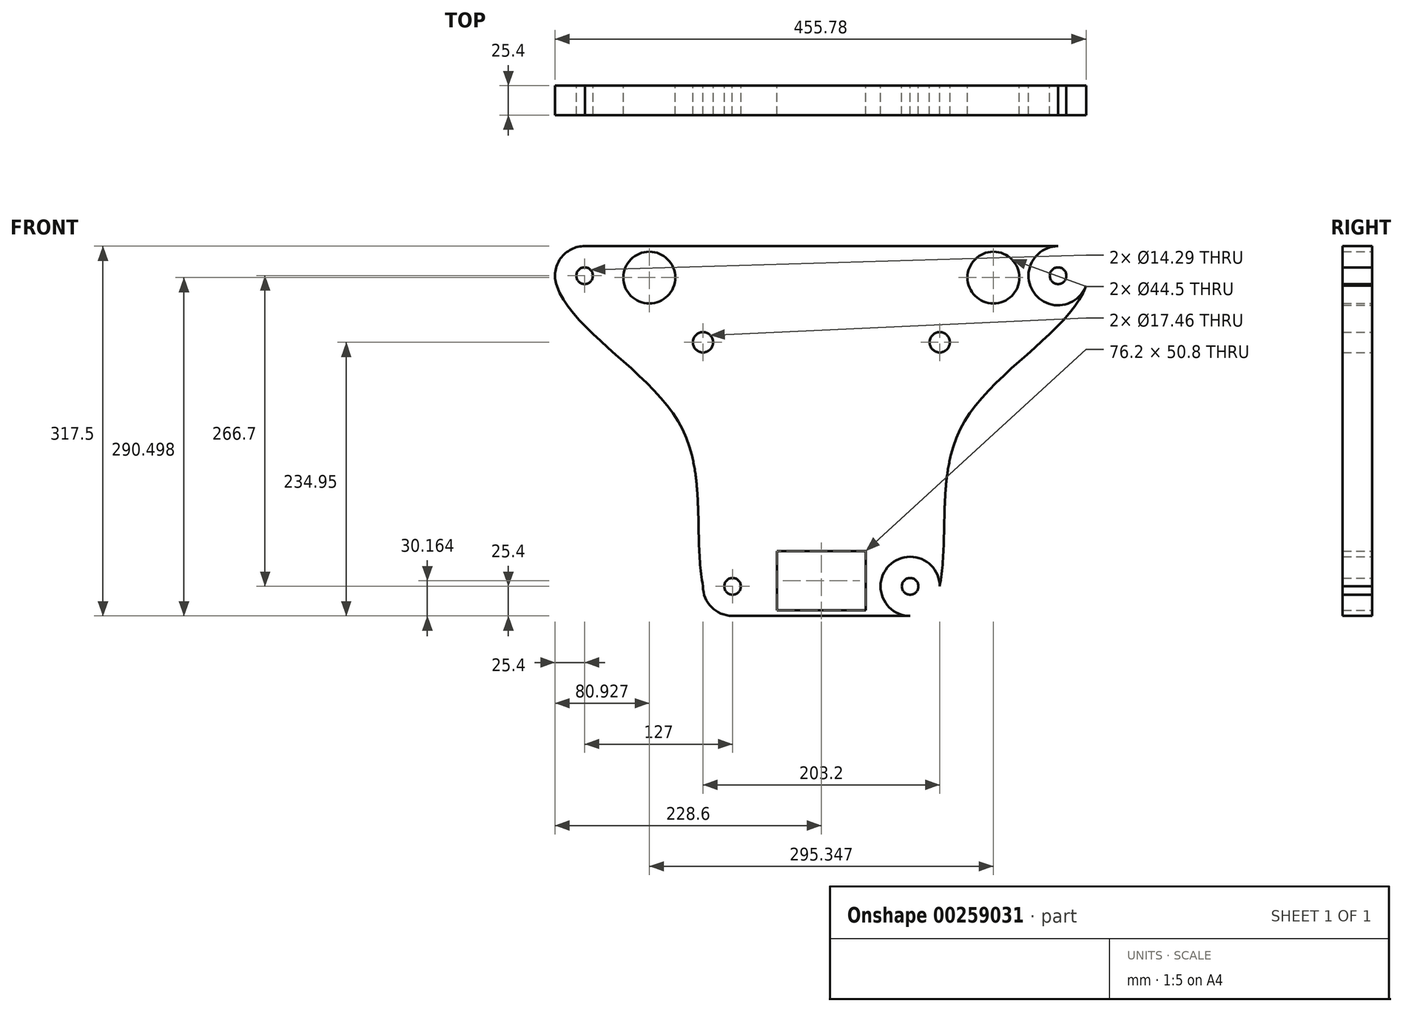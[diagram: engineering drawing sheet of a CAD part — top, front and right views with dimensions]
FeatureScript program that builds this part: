
annotation { "Feature Type Name" : "Feature", "Feature Type Description" : "" }
export const myFeature = defineFeature(function(context is Context, id is Id, definition is map)
    precondition{}
    {
        {
            var Q0;
            Q0=qCreatedBy(makeId("Front.planeOp"),FACE);
            var sketch = newSketch(context, id + "F0", { "sketchPlane" : qUnion([Q0])});
            skCircle(sketch, "E0", {"center": v(-203.2, 126.33) * mm, "radius": 7.14 * mm});
            skCircle(sketch, "E1", {"center": v(-76.2, -140.37) * mm, "radius": 7.14 * mm});
            skCircle(sketch, "E2.MirrorC", {"center": v(203.2, 126.33) * mm, "radius": 7.14 * mm});
            skCircle(sketch, "E3.MirrorC", {"center": v(76.2, -140.37) * mm, "radius": 7.14 * mm});
            skCircle(sketch, "E4", {"center": v(-203.2, 126.33) * mm, "radius": 25.4 * mm});
            skCircle(sketch, "E5", {"center": v(-76.2, -140.37) * mm, "radius": 25.4 * mm});
            skFitSpline(sketch, "E6", {"points": [v(-227.18, 117.96) * mm, v(-122.19, 0) * mm, v(-101.6, -140.28) * mm], "startDerivative": vector(79.1, -228.7) * mm, "endDerivative": vector(52.2, -286.58) * mm});
            skCircle(sketch, "E7.MirrorC", {"center": v(203.2, 126.33) * mm, "radius": 25.4 * mm});
            skCircle(sketch, "E8.MirrorC", {"center": v(76.2, -140.37) * mm, "radius": 25.4 * mm});
            skFitSpline(sketch, "E9.MirrorCS", {"points": [v(227.18, 117.96) * mm, v(122.19, 0) * mm, v(101.6, -140.28) * mm], "startDerivative": vector(-79.1, -228.7) * mm, "endDerivative": vector(-52.2, -286.58) * mm});
            skLineSegment(sketch, "E10", {"start": v(-202.87, 151.73) * mm, "end": v(203.2, 151.73) * mm});
            skLineSegment(sketch, "E11.bottom", {"start": v(38.1, -161) * mm, "end": v(-38.1, -161) * mm});
            skLineSegment(sketch, "E11.top", {"start": v(38.1, -110.2) * mm, "end": v(-38.1, -110.2) * mm});
            skLineSegment(sketch, "E11.left", {"start": v(38.1, -161) * mm, "end": v(38.1, -110.2) * mm});
            skLineSegment(sketch, "E11.right", {"start": v(-38.1, -161) * mm, "end": v(-38.1, -110.2) * mm});
            skPoint(sketch, "E11.middle", {"position": v(0, -135.6) * mm});
            skCircle(sketch, "E12", {"center": v(-147.67, 124.73) * mm, "radius": 22.25 * mm});
            skCircle(sketch, "E13.MirrorC", {"center": v(147.67, 124.73) * mm, "radius": 22.25 * mm});
            skCircle(sketch, "E14", {"center": v(-101.6, -64.17) * mm, "radius": 7.15 * mm});
            skLineSegment(sketch, "E15.bottom", {"start": v(133.35, -78.46) * mm, "end": v(-133.35, -78.46) * mm});
            skLineSegment(sketch, "E15.top", {"start": v(158.75, -27.66) * mm, "end": v(-158.75, -27.66) * mm});
            skLineSegment(sketch, "E15.left", {"start": v(165.1, -46.7) * mm, "end": v(165.1, -34) * mm});
            skLineSegment(sketch, "E15.right", {"start": v(-165.1, -46.7) * mm, "end": v(-165.1, -34) * mm});
            skPoint(sketch, "E15.middle", {"position": v(0, -53.06) * mm});
            skCircle(sketch, "E16", {"center": v(-138.22, -45.44) * mm, "radius": 7.15 * mm});
            skPoint(sketch, "E17.visualSharp", {"position": v(-165.1, -78.46) * mm});
            skArc(sketch, "E17.filletArc", {"start": v(-165.1, -46.7) * mm, "mid": v(-155.8, -69.16) * mm, "end": v(-133.35, -78.46) * mm});
            skCircle(sketch, "E18.MirrorC", {"center": v(101.6, -64.17) * mm, "radius": 7.15 * mm});
            skCircle(sketch, "E19.MirrorC", {"center": v(138.22, -45.44) * mm, "radius": 7.15 * mm});
            skArc(sketch, "E20.MirrorCS", {"start": v(165.1, -46.7) * mm, "mid": v(155.8, -69.16) * mm, "end": v(133.35, -78.46) * mm});
            skPoint(sketch, "E21.visualSharp", {"position": v(-165.1, -27.66) * mm});
            skArc(sketch, "E21.filletArc", {"start": v(-158.75, -27.66) * mm, "mid": v(-163.24, -29.52) * mm, "end": v(-165.1, -34) * mm});
            skArc(sketch, "E22.MirrorCS", {"start": v(158.75, -27.66) * mm, "mid": v(163.24, -29.52) * mm, "end": v(165.1, -34) * mm});
            skPoint(sketch, "E23.orphan", {"position": v(165.1, -78.46) * mm});
            skPoint(sketch, "E24.orphan", {"position": v(165.1, -27.66) * mm});
            skLineSegment(sketch, "E25", {"start": v(-138.22, -45.44) * mm, "end": v(-764.67, -149.3) * mm});
            skLineSegment(sketch, "E26.MirrorCS", {"start": v(138.22, -45.44) * mm, "end": v(764.67, -149.3) * mm});
            skCircle(sketch, "E27", {"center": v(-101.6, 69.18) * mm, "radius": 8.73 * mm});
            skCircle(sketch, "E28.MirrorC", {"center": v(101.6, 69.18) * mm, "radius": 8.73 * mm});
            skLineSegment(sketch, "E29", {"start": v(-76.47, -165.77) * mm, "end": v(76.2, -165.77) * mm});
            skSolve(sketch);
        }
        {
            var Q0;
            {var subQ8=sQuery(id+"F0.wireOp",EDGE,"E10");Q0=makeQuery(id+"F0.imprint","IMPRINT",FACE,{"disambiguationData":[TD([[makeQuery(id+"F0.imprint","IMPRINT",EDGE,{"derivedFrom":subQ8}),-1.0]])]});}
            var Q1;
            Q1=makeQuery(id+"F0.imprint","IMPRINT",FACE,{"disambiguationData":[TD([[makeQuery(id+"F0.imprint","IMPRINT",EDGE,{"derivedFrom":sQuery(id+"F0.wireOp",EDGE,"E2.MirrorC")}),1.0]])]});
            var Q2;
            Q2=makeQuery(id+"F0.imprint","IMPRINT",FACE,{"disambiguationData":[TD([[makeQuery(id+"F0.imprint","IMPRINT",EDGE,{"derivedFrom":sQuery(id+"F0.wireOp",EDGE,"E0")}),-1.0]])]});
            var Q3;
            Q3=makeQuery(id+"F0.imprint","IMPRINT",FACE,{"disambiguationData":[TD([[makeQuery(id+"F0.imprint","IMPRINT",EDGE,{"derivedFrom":sQuery(id+"F0.wireOp",EDGE,"E11.bottom")}),1.0]])]});
            var Q4;
            Q4=makeQuery(id+"F0.imprint","IMPRINT",FACE,{"disambiguationData":[TD([[makeQuery(id+"F0.imprint","IMPRINT",EDGE,{"derivedFrom":sQuery(id+"F0.wireOp",EDGE,"E1")}),-1.0]])]});
            var Q5;
            Q5=makeQuery(id+"F0.imprint","IMPRINT",FACE,{"disambiguationData":[TD([[makeQuery(id+"F0.imprint","IMPRINT",EDGE,{"derivedFrom":sQuery(id+"F0.wireOp",EDGE,"E3.MirrorC")}),1.0]])]});
            var Q6;
            {var subQ5=sQuery(id+"F0.wireOp",EDGE,"E15.top");var subQ6=sQuery(id+"F0.wireOp",EDGE,"E6");var subQ7=makeQuery(id+"F0.imprint","INTERSECT",VERTEX,{"derivedFrom":[subQ6,subQ5]});Q6=makeQuery(id+"F0.imprint","IMPRINT",FACE,{"disambiguationData":[TD([[makeQuery(id+"F0.imprint","IMPRINT",EDGE,{"disambiguationData":[TD([[subQ7,-1.0]])],"derivedFrom":subQ6}),1.0]])]});}
            var Q7;
            {var subQ0=sQuery(id+"F0.wireOp",EDGE,"E14");var subQ1=sQuery(id+"F0.wireOp",EDGE,"E6");var subQ2=makeQuery(id+"F0.imprint","INTERSECT",VERTEX,{"disambiguationData":[OD(0.0)],"derivedFrom":[subQ1,subQ0]});Q7=makeQuery(id+"F0.imprint","IMPRINT",FACE,{"disambiguationData":[TD([[makeQuery(id+"F0.imprint","IMPRINT",EDGE,{"disambiguationData":[TD([[subQ2,-1.0]])],"derivedFrom":subQ1}),1.0]])]});}
            var Q8;
            {var subQ0=sQuery(id+"F0.wireOp",EDGE,"E18.MirrorC");var subQ1=sQuery(id+"F0.wireOp",EDGE,"E9.MirrorCS");var subQ2=makeQuery(id+"F0.imprint","INTERSECT",VERTEX,{"disambiguationData":[OD(0.0)],"derivedFrom":[subQ1,subQ0]});Q8=makeQuery(id+"F0.imprint","IMPRINT",FACE,{"disambiguationData":[TD([[makeQuery(id+"F0.imprint","IMPRINT",EDGE,{"disambiguationData":[TD([[subQ2,-1.0]])],"derivedFrom":subQ1}),-1.0]])]});}
            extrude(context, id + "F1", {"entities" : qUnion([Q0, Q1, Q2, Q3, Q4, Q5, Q6, Q7, Q8]), "depth" : 25.4 * mm});
        }
    });
